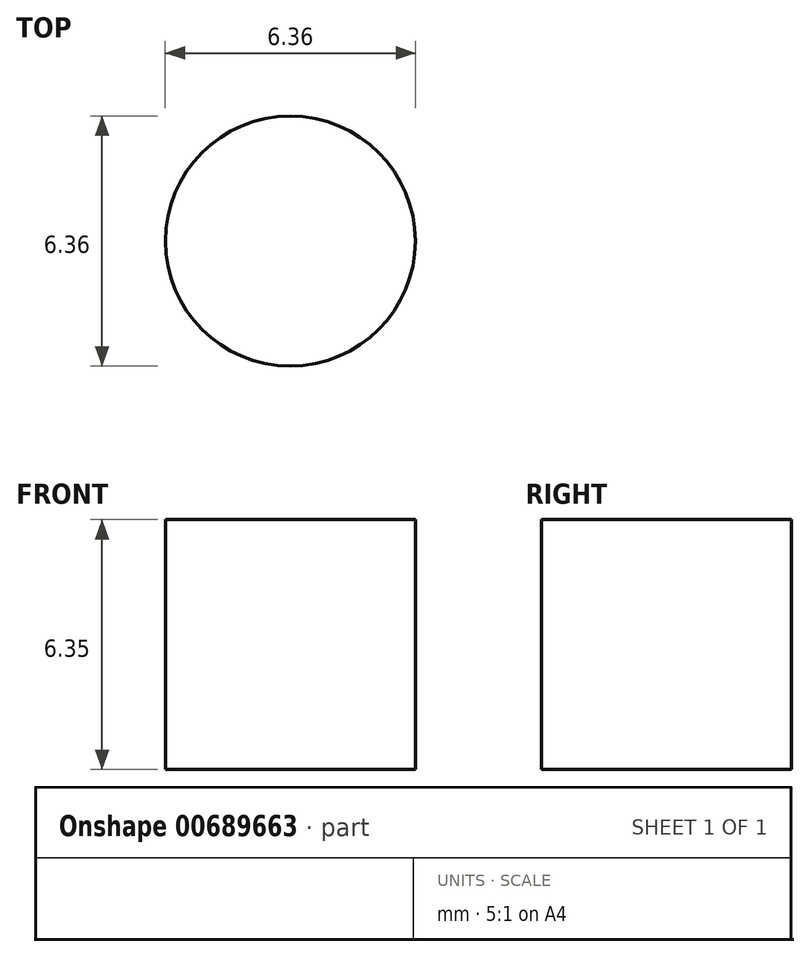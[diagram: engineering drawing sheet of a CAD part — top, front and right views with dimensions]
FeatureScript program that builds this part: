
annotation { "Feature Type Name" : "Feature", "Feature Type Description" : "" }
export const myFeature = defineFeature(function(context is Context, id is Id, definition is map)
    precondition{}
    {
        {
            var Q0;
            Q0=qCreatedBy(makeId("Top.planeOp"),FACE);
            var sketch = newSketch(context, id + "F0", { "sketchPlane" : qUnion([Q0])});
            skCircle(sketch, "E0", {"center": v(0, 0) * mm, "radius": 3.18 * mm});
            skSolve(sketch);
        }
        {
            var Q0;
            Q0 = qSketchRegion(id + "F0", true);
            extrude(context, id + "F1", {"entities" : qUnion([Q0]), "depth" : 6.35 * mm, "offsetDistance" : 25.4 * mm});
        }
    });
